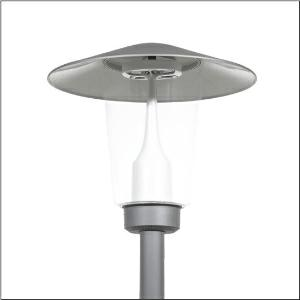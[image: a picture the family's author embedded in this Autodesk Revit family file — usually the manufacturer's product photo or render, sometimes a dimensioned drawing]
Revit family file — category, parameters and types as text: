
# Revit family: pilzleuchte_iq___p1_0a_5xa5235lf14hp_c758
name_source: partatom
category: Lighting Fixtures
units: mm (PartAtom-declared; Revit-internal decimal feet)

## family parameters
Cut with Voids When Loaded = No
Host = Face
Light Source = No
Part Type = Normal
Room Calculation Point = No
Round Connector Dimension = Use Diameter
Shared = No

## types (1)
- --- (1 x LED, 4960 lm, 33.6 W, 4000K)
    Apparent Load = 34 VA
    CIE Flux Codes = 35 64 90 96 100
    Color Rendering = 70
    Color Temperature = 4000K
    Default Elevation = 1800 mm
    Description = Mushroom Luminaire iQ, mast luminaire, Module 540 iQ-SR, primary light control with 3 zone facetted reflector, of plastic, silver coated, highly specular, structured, primary optical cover: cover, of PMMA, transparent, light distribution: P1.0a, light emission: direct distribution, primary light characteristic: strongly asymmetric, installation type: post-top, LED, High Power LED, rated luminous flux: 4.960lm, luminous efficacy: 148lm/W, light colour: 740, colour temperature: 4000K, control gear: ECG iQ, control: pre-setting: logarithmic dimming characteristic, Street-Remote, Auto-Match, Temp-Guard, Lumen-Switch, Night-Set, Smart-Wire, Light-Fading, Desk-Remote (wireless, voltage-free reading and setting of iQ features in the workshop via application-optimized NFC function/RFID function), optimised constant luminous flux control (CLO 2.0), with terminal, 6-pole, max. 2.5mm², mains connection: 230..240V, AC, 50/60Hz, start of lifetime: 34W, end of service life: 36W, reduction: 15W, luminaire housing, upper part, of glass-fibre reinforced polyester, coated, Siteco® metallic grey (DB 702S), diameter: 650mm, height: 586mm, spigot size: d x l = 76 x 70mm (post-top) | with reducer (optional accessory) 60 x 70mm, post-top mast mounting element, of diecast aluminium, coated, Siteco® metallic grey (DB 702S), Module 540 iQ-SR, traffic white (RAL 9016), equipment: Power, protection rating (complete): IP65, insulation class (complete): insulation class II (safety insulation), certification: CE, ENEC, VDE, packaging unit: 1 piece

Light Distribution: P1.0a
    Height = 586 mm
    Lamp = 1 x LED
    Lamp Light Flux = 4960 lm
    Lamp Power = 33.6 W
    Lamp count = 1
    Length = 650 mm
    Luminous efficacy = 148 lm/W
    Manufacturer = Siteco
    ModVariant = No
    Model = 5XA5235LF14HP
    Number of Poles = 1
    OnlyDefault = Yes
    Power Factor = 1
    Product Name = Pilzleuchte iQ | P1.0a
    Product group = mast luminaire | pylon top
    ProductGroupID = 6100
    Protection Class = Protection class II
    Protection Degree = IP 65
    RLX_Detail_Level = 1
    RLX_Emergency_Light_Flux = 0 lm
    RLX_Emergency_Type = 0
    RLX_Emergency_Type_DB = No
    RlxData = <blob elided: 52093 chars, md5=27f1d679>
    Socket = socket
    Standby Power = 0 W
    System Light Flux = 4960 lm
    System Power = 34 W
    Type Comments = factory setting: luminous flux: 100 % | dim-lin: 254 | 695 mA
    Type Image = l_1006077.jpg
    URL = http://relux.com
    VarID = @adj_164791
    Voltage = 0 V
    Weight = 0.00 kg
    Width = 0 mm  [stored 0 ft]

note: [stored X ft] marks values corroborated as IEEE doubles in the binary element streams (Revit-internal decimal feet)

## geometry (parser evidence)
native form markers: Blend x4, Sweep x13
no freeform markers — native parametric forms only
